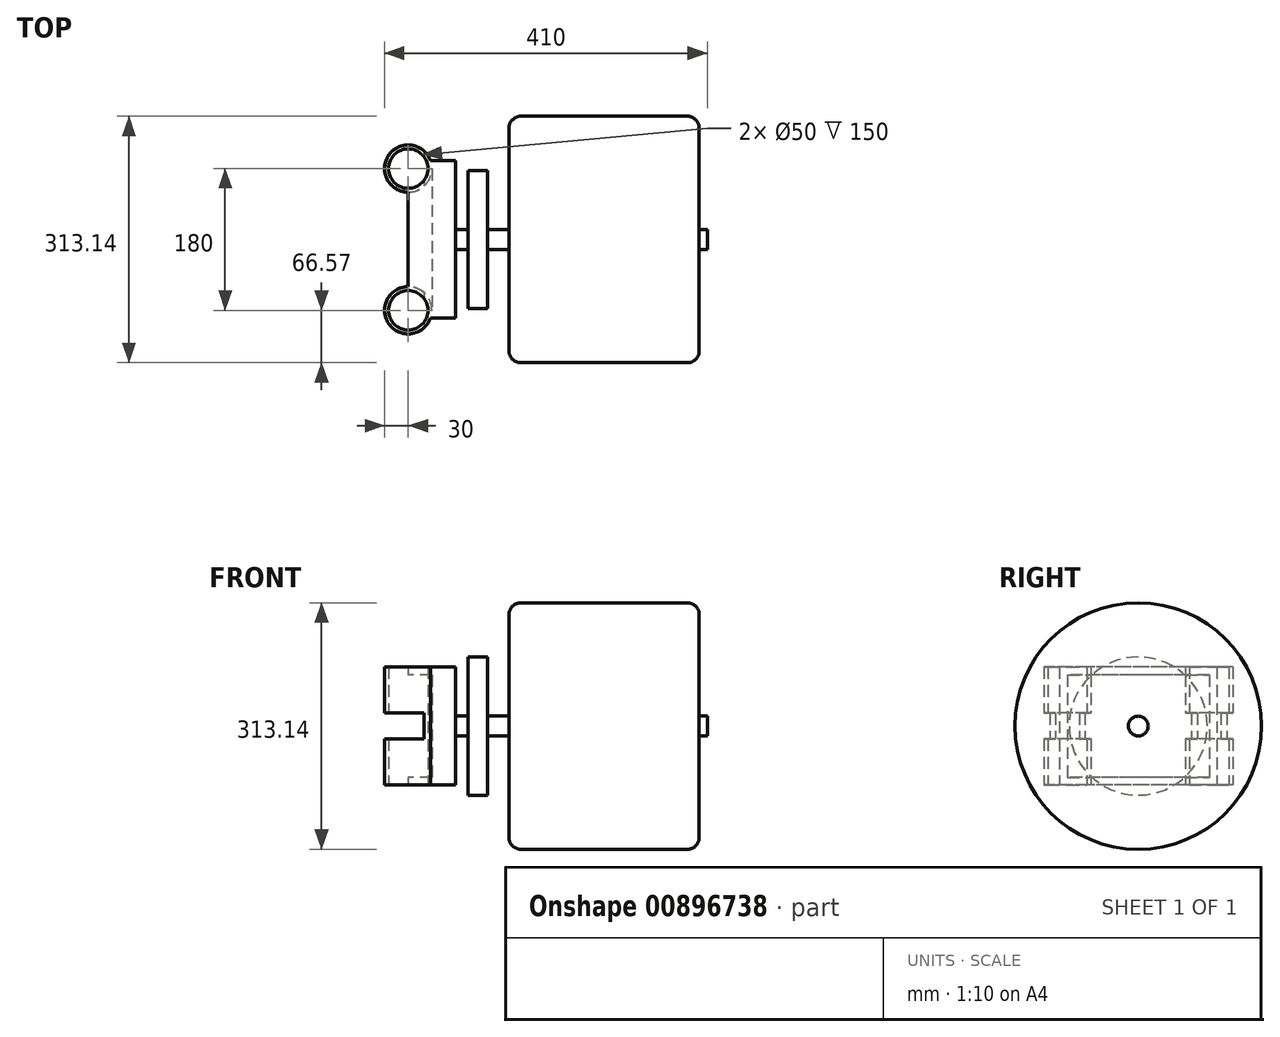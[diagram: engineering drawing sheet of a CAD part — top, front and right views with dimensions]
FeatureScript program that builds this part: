
annotation { "Feature Type Name" : "Feature", "Feature Type Description" : "" }
export const myFeature = defineFeature(function(context is Context, id is Id, definition is map)
    precondition{}
    {
        {
            var Q0;
            Q0=qCreatedBy(makeId("Top.planeOp"),FACE);
            var sketch = newSketch(context, id + "F0", { "sketchPlane" : qUnion([Q0])});
            skLineSegment(sketch, "E0.bottom", {"start": v(-30, 100) * mm, "end": v(30, 100) * mm});
            skLineSegment(sketch, "E0.top", {"start": v(-30, -100) * mm, "end": v(30, -100) * mm});
            skLineSegment(sketch, "E0.left", {"start": v(-30, 100) * mm, "end": v(-30, -100) * mm});
            skLineSegment(sketch, "E0.right", {"start": v(30, 100) * mm, "end": v(30, -100) * mm});
            skPoint(sketch, "E0.middle", {"position": v(0, 0) * mm});
            skLineSegment(sketch, "E1.bottom", {"start": v(71, 87.8) * mm, "end": v(45.75, 87.8) * mm});
            skLineSegment(sketch, "E1.left", {"start": v(71, 87.8) * mm, "end": v(71, 0) * mm});
            skLineSegment(sketch, "E1.right", {"start": v(45.75, 87.8) * mm, "end": v(45.75, 0) * mm});
            skPoint(sketch, "E1.middle", {"position": v(58.38, 0) * mm});
            skLineSegment(sketch, "E2.bottom", {"start": v(98.04, 156.57) * mm, "end": v(339.61, 156.57) * mm});
            skLineSegment(sketch, "E2.left", {"start": v(98.04, 156.57) * mm, "end": v(98.04, 0) * mm});
            skLineSegment(sketch, "E2.right", {"start": v(339.61, 156.57) * mm, "end": v(339.61, 0) * mm});
            skPoint(sketch, "E2.middle", {"position": v(218.83, 0) * mm});
            skPoint(sketch, "E2.top.end.orphan", {"position": v(339.61, -156.57) * mm});
            skPoint(sketch, "E2.top.start.orphan", {"position": v(98.04, -156.57) * mm});
            skPoint(sketch, "E3.endSnap0", {"position": v(30, 0) * mm});
            skPoint(sketch, "E1.top.end.orphan", {"position": v(45.75, -87.8) * mm});
            skPoint(sketch, "E1.top.start.orphan", {"position": v(71, -87.8) * mm});
            skLineSegment(sketch, "E4", {"start": v(45.75, 0) * mm, "end": v(71, 0) * mm});
            skLineSegment(sketch, "E5", {"start": v(98.04, 0) * mm, "end": v(339.61, 0) * mm});
            skSolve(sketch);
        }
        {
            var Q0;
            Q0=makeQuery(id+"F0.imprint","IMPRINT",FACE,{"disambiguationData":[TD([[makeQuery(id+"F0.imprint","IMPRINT",EDGE,{"derivedFrom":sQuery(id+"F0.wireOp",EDGE,"E1.bottom")}),1.0]])]});
            var Q1;
            Q1=sQuery(id+"F0.wireOp",EDGE,"E4");
            revolve(context, id + "F1", {"surfaceOperationType" : NewSurfaceOperationType.NEW, "entities" : qUnion([Q0]), "axis" : qUnion([Q1]), "revolveType" : RevolveType.FULL});
        }
        {
            var Q0;
            Q0=makeQuery(id+"F0.imprint","IMPRINT",FACE,{"disambiguationData":[TD([[makeQuery(id+"F0.imprint","IMPRINT",EDGE,{"derivedFrom":sQuery(id+"F0.wireOp",EDGE,"E2.bottom")}),-1.0]])]});
            var Q1;
            Q1=sQuery(id+"F0.wireOp",EDGE,"E5");
            revolve(context, id + "F2", {"surfaceOperationType" : NewSurfaceOperationType.NEW, "entities" : qUnion([Q0]), "axis" : qUnion([Q1]), "revolveType" : RevolveType.FULL});
        }
        {
            var Q0;
            Q0=qCreatedBy(makeId("Right.planeOp"),FACE);
            var sketch = newSketch(context, id + "F3", { "sketchPlane" : qUnion([Q0])});
            skCircle(sketch, "E6", {"center": v(0, 0) * mm, "radius": 12.57 * mm});
            skSolve(sketch);
        }
        {
            var Q0;
            Q0=makeQuery(id+"F0.imprint","IMPRINT",FACE,{"disambiguationData":[TD([[makeQuery(id+"F0.imprint","IMPRINT",EDGE,{"derivedFrom":sQuery(id+"F0.wireOp",EDGE,"E0.bottom")}),-1.0]])]});
            extrude(context, id + "F4", {"entities" : qUnion([Q0]), "endBound" : BoundingType.SYMMETRIC, "depth" : 150 * mm, "offsetDistance" : 25 * mm});
        }
        {
            var Q0;
            Q0 = qSketchRegion(id + "F3", true);
            extrude(context, id + "F5", {"entities" : qUnion([Q0]), "operationType" : NewBodyOperationType.REMOVE, "endBound" : BoundingType.SYMMETRIC, "depth" : 10000 * mm, "offsetDistance" : 25 * mm});
        }
        {
            var Q0;
            Q0=qCreatedBy(makeId("Right.planeOp"),FACE);
            var sketch = newSketch(context, id + "F6", { "sketchPlane" : qUnion([Q0])});
            skLineSegment(sketch, "E7.bottom", {"start": v(90, 65) * mm, "end": v(-90, 65) * mm});
            skLineSegment(sketch, "E7.top", {"start": v(90, -65) * mm, "end": v(-90, -65) * mm});
            skLineSegment(sketch, "E7.left", {"start": v(90, 65) * mm, "end": v(90, -65) * mm});
            skLineSegment(sketch, "E7.right", {"start": v(-90, 65) * mm, "end": v(-90, -65) * mm});
            skPoint(sketch, "E7.middle", {"position": v(0, 0) * mm});
            skSolve(sketch);
        }
        {
            var Q0;
            Q0 = qSketchRegion(id + "F6", true);
            extrude(context, id + "F7", {"entities" : qUnion([Q0]), "operationType" : NewBodyOperationType.REMOVE, "oppositeDirection" : true, "depth" : 6000 * mm, "offsetDistance" : 25 * mm});
        }
        {
            var Q0;
            Q0=qCreatedBy(makeId("Top.planeOp"),FACE);
            var sketch = newSketch(context, id + "F8", { "sketchPlane" : qUnion([Q0])});
            skLineSegment(sketch, "E8", {"start": v(35.94, 0) * mm, "end": v(-85.78, 0) * mm, "construction": true});
            skLineSegment(sketch, "E9", {"start": v(-30, 0) * mm, "end": v(-30, 119.58) * mm, "construction": true});
            skCircle(sketch, "E10", {"center": v(-30, 90) * mm, "radius": 30 * mm});
            skLineSegment(sketch, "E11", {"start": v(-30, 0) * mm, "end": v(-30, -180) * mm, "construction": true});
            skCircle(sketch, "E12", {"center": v(-30, -90) * mm, "radius": 30 * mm});
            skCircle(sketch, "E13", {"center": v(-30, 90) * mm, "radius": 25 * mm});
            skCircle(sketch, "E14", {"center": v(-30, -90) * mm, "radius": 25 * mm});
            skSolve(sketch);
        }
        {
            var Q0;
            Q0=makeQuery(id+"F8.imprint","IMPRINT",FACE,{"disambiguationData":[TD([[makeQuery(id+"F8.imprint","IMPRINT",EDGE,{"derivedFrom":sQuery(id+"F8.wireOp",EDGE,"E10")}),1.0]])]});
            var Q1;
            Q1=makeQuery(id+"F8.imprint","IMPRINT",FACE,{"disambiguationData":[TD([[makeQuery(id+"F8.imprint","IMPRINT",EDGE,{"derivedFrom":sQuery(id+"F8.wireOp",EDGE,"E12")}),1.0]])]});
            extrude(context, id + "F9", {"entities" : qUnion([Q0, Q1]), "operationType" : NewBodyOperationType.ADD, "endBound" : BoundingType.SYMMETRIC, "depth" : 150 * mm, "offsetDistance" : 25 * mm});
        }
        {
            var Q0;
            Q0=qCreatedBy(makeId("Right.planeOp"),FACE);
            cPlane(context, id + "F10", {"entities" : qUnion([Q0]), "cplaneType" : CPlaneType.OFFSET, "offset" : 10 * mm, "oppositeDirection" : true, "width" : 150 * mm, "height" : 150 * mm});
        }
        {
            var Q0;
            Q0=qCreatedBy(id+"F10.planeOp",FACE);
            var sketch = newSketch(context, id + "F11", { "sketchPlane" : qUnion([Q0])});
            skLineSegment(sketch, "E15.bottom", {"start": v(20000, 16.5) * mm, "end": v(-20000, 16.5) * mm});
            skLineSegment(sketch, "E15.top", {"start": v(20000, -16.5) * mm, "end": v(-20000, -16.5) * mm});
            skLineSegment(sketch, "E15.left", {"start": v(20000, 16.5) * mm, "end": v(20000, -16.5) * mm});
            skLineSegment(sketch, "E15.right", {"start": v(-20000, 16.5) * mm, "end": v(-20000, -16.5) * mm});
            skPoint(sketch, "E15.middle", {"position": v(0, 0) * mm});
            skSolve(sketch);
        }
        {
            var Q0;
            Q0 = qSketchRegion(id + "F11", true);
            extrude(context, id + "F12", {"entities" : qUnion([Q0]), "operationType" : NewBodyOperationType.REMOVE, "oppositeDirection" : true, "depth" : 15000 * mm, "offsetDistance" : 25 * mm});
        }
        {
            var Q0;
            Q0=makeQuery(id+"F8.imprint","IMPRINT",FACE,{"disambiguationData":[TD([[makeQuery(id+"F8.imprint","IMPRINT",EDGE,{"derivedFrom":sQuery(id+"F8.wireOp",EDGE,"E13")}),1.0]])]});
            extrude(context, id + "F13", {"entities" : qUnion([Q0]), "operationType" : NewBodyOperationType.REMOVE, "endBound" : BoundingType.SYMMETRIC, "oppositeDirection" : true, "depth" : 2000 * mm, "offsetDistance" : 25 * mm});
        }
        {
            var Q0;
            Q0=makeQuery(id+"F8.imprint","IMPRINT",FACE,{"disambiguationData":[TD([[makeQuery(id+"F8.imprint","IMPRINT",EDGE,{"derivedFrom":sQuery(id+"F8.wireOp",EDGE,"E14")}),1.0]])]});
            extrude(context, id + "F14", {"entities" : qUnion([Q0]), "operationType" : NewBodyOperationType.REMOVE, "endBound" : BoundingType.SYMMETRIC, "oppositeDirection" : true, "depth" : 2000 * mm, "offsetDistance" : 25 * mm});
        }
        {
            var Q0;
            Q0 = qSketchRegion(id + "F3", true);
            extrude(context, id + "F15", {"entities" : qUnion([Q0]), "operationType" : NewBodyOperationType.ADD, "depth" : 350 * mm, "offsetDistance" : 25 * mm});
        }
        {
            var Q0;
            Q0=makeQuery(id+"F2.opRevolve","SWEPT_EDGE",EDGE,{"disambiguationData":[OSD([sQuery(id+"F0.wireOp",EDGE,"E2.bottom"),sQuery(id+"F0.wireOp",EDGE,"E2.right")])]});
            var Q1;
            Q1=makeQuery(id+"F2.opRevolve","SWEPT_EDGE",EDGE,{"disambiguationData":[OSD([sQuery(id+"F0.wireOp",EDGE,"E2.bottom"),sQuery(id+"F0.wireOp",EDGE,"E2.left")])]});
            fillet(context, id + "F16", {"entities" : qUnion([Q0, Q1]), "radius" : 15 * mm, "tangentPropagation" : true, "allowEdgeOverflow" : false});
        }
    });
